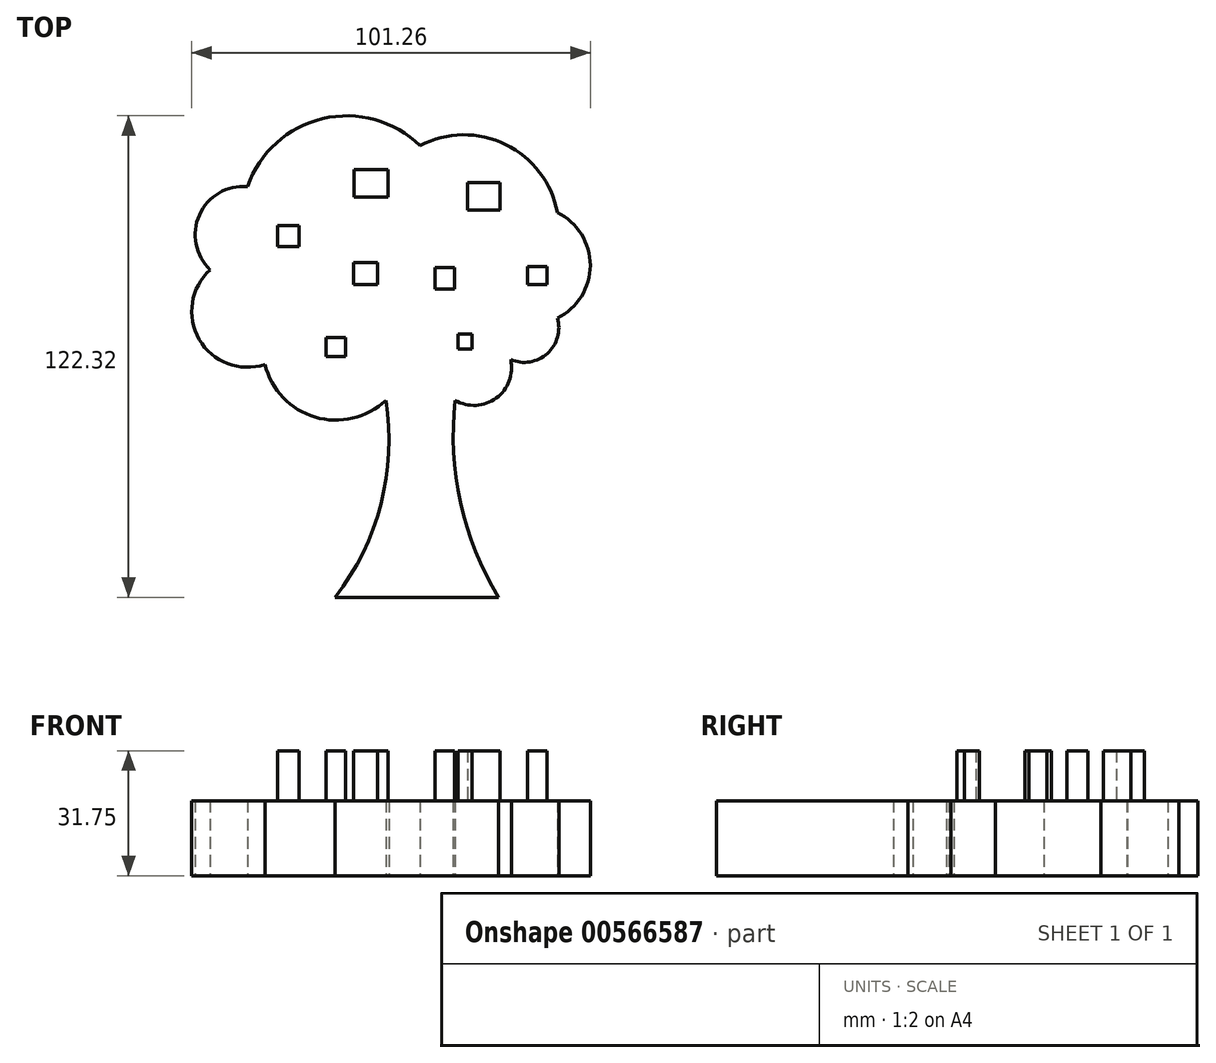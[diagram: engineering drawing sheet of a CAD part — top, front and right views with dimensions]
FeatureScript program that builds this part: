
annotation { "Feature Type Name" : "Feature", "Feature Type Description" : "" }
export const myFeature = defineFeature(function(context is Context, id is Id, definition is map)
    precondition{}
    {
        {
            var Q0;
            Q0=qCreatedBy(makeId("Top.planeOp"),FACE);
            var sketch = newSketch(context, id + "F0", { "sketchPlane" : qUnion([Q0])});
            skArc(sketch, "E0", {"start": v(-21.58, -70.95) * mm, "mid": v(-9.97, -47.28) * mm, "end": v(-8.71, -20.95) * mm});
            skArc(sketch, "E1", {"start": v(8.92, -20.95) * mm, "mid": v(10.25, -46.87) * mm, "end": v(19.92, -70.95) * mm});
            skLineSegment(sketch, "E2", {"start": v(-21.58, -70.95) * mm, "end": v(19.92, -70.95) * mm});
            skArc(sketch, "E3", {"start": v(-39.42, -11.83) * mm, "mid": v(-26.68, -25.19) * mm, "end": v(-8.71, -20.95) * mm});
            skArc(sketch, "E4", {"start": v(-53.32, 12.24) * mm, "mid": v(-56.13, -5.43) * mm, "end": v(-39.42, -11.83) * mm});
            skArc(sketch, "E5", {"start": v(-43.83, 33.4) * mm, "mid": v(-56.09, 26.19) * mm, "end": v(-53.32, 12.24) * mm});
            skArc(sketch, "E6", {"start": v(0, 43.77) * mm, "mid": v(-24.77, 50.66) * mm, "end": v(-43.83, 33.4) * mm});
            skArc(sketch, "E7", {"start": v(34.85, 26.76) * mm, "mid": v(21.74, 44.1) * mm, "end": v(0, 43.77) * mm});
            skArc(sketch, "E8", {"start": v(34.85, 0) * mm, "mid": v(43.23, 13.38) * mm, "end": v(34.85, 26.76) * mm});
            skArc(sketch, "E9", {"start": v(23.03, -10.58) * mm, "mid": v(32.3, -9.04) * mm, "end": v(34.85, 0) * mm});
            skArc(sketch, "E10", {"start": v(8.92, -20.95) * mm, "mid": v(19.33, -20.33) * mm, "end": v(23.03, -10.58) * mm});
            skSolve(sketch);
        }
        {
            var Q0;
            Q0 = qSketchRegion(id + "F0", true);
            extrude(context, id + "F1", {"entities" : qUnion([Q0]), "depth" : 19.05 * mm, "offsetDistance" : 25.4 * mm});
        }
        {
            var Q0;
            Q0=makeQuery(id+"F1.opExtrude","CAP_FACE",FACE,{"disambiguationData":[OSD([sQuery(id+"F0.wireOp",EDGE,"E0"),sQuery(id+"F0.wireOp",EDGE,"E1"),sQuery(id+"F0.wireOp",EDGE,"E2"),sQuery(id+"F0.wireOp",EDGE,"E3"),sQuery(id+"F0.wireOp",EDGE,"E4"),sQuery(id+"F0.wireOp",EDGE,"E5"),sQuery(id+"F0.wireOp",EDGE,"E6"),sQuery(id+"F0.wireOp",EDGE,"E7"),sQuery(id+"F0.wireOp",EDGE,"E8"),sQuery(id+"F0.wireOp",EDGE,"E9"),sQuery(id+"F0.wireOp",EDGE,"E10")])],"isStart":false});
            var sketch = newSketch(context, id + "F2", { "sketchPlane" : qUnion([Q0])});
            skLineSegment(sketch, "E11.bottom", {"start": v(-30.77, 18.09) * mm, "end": v(-36.17, 18.09) * mm});
            skLineSegment(sketch, "E11.top", {"start": v(-30.77, 23.48) * mm, "end": v(-36.17, 23.48) * mm});
            skLineSegment(sketch, "E11.left", {"start": v(-30.77, 18.09) * mm, "end": v(-30.77, 23.48) * mm});
            skLineSegment(sketch, "E11.right", {"start": v(-36.17, 18.09) * mm, "end": v(-36.17, 23.48) * mm});
            skPoint(sketch, "E11.middle", {"position": v(-33.47, 20.78) * mm});
            skLineSegment(sketch, "E12.bottom", {"start": v(8.73, 12.81) * mm, "end": v(3.82, 12.81) * mm});
            skLineSegment(sketch, "E12.top", {"start": v(8.73, 7.41) * mm, "end": v(3.82, 7.41) * mm});
            skLineSegment(sketch, "E12.left", {"start": v(8.73, 12.81) * mm, "end": v(8.73, 7.41) * mm});
            skLineSegment(sketch, "E12.right", {"start": v(3.82, 12.81) * mm, "end": v(3.82, 7.41) * mm});
            skPoint(sketch, "E12.middle", {"position": v(6.28, 10.11) * mm});
            skLineSegment(sketch, "E13.bottom", {"start": v(20.33, 27.38) * mm, "end": v(12.03, 27.38) * mm});
            skLineSegment(sketch, "E13.top", {"start": v(20.33, 34.44) * mm, "end": v(12.03, 34.44) * mm});
            skLineSegment(sketch, "E13.left", {"start": v(20.33, 27.38) * mm, "end": v(20.33, 34.44) * mm});
            skLineSegment(sketch, "E13.right", {"start": v(12.03, 27.38) * mm, "end": v(12.03, 34.44) * mm});
            skPoint(sketch, "E13.middle", {"position": v(16.18, 30.91) * mm});
            skLineSegment(sketch, "E14.bottom", {"start": v(-8.1, 37.76) * mm, "end": v(-16.8, 37.76) * mm});
            skLineSegment(sketch, "E14.top", {"start": v(-8.1, 30.7) * mm, "end": v(-16.8, 30.7) * mm});
            skLineSegment(sketch, "E14.left", {"start": v(-8.1, 37.76) * mm, "end": v(-8.1, 30.7) * mm});
            skLineSegment(sketch, "E14.right", {"start": v(-16.8, 37.76) * mm, "end": v(-16.8, 30.7) * mm});
            skPoint(sketch, "E14.middle", {"position": v(-12.45, 34.23) * mm});
            skLineSegment(sketch, "E15.bottom", {"start": v(-18.91, -9.8) * mm, "end": v(-23.87, -9.8) * mm});
            skLineSegment(sketch, "E15.top", {"start": v(-18.91, -4.98) * mm, "end": v(-23.87, -4.98) * mm});
            skLineSegment(sketch, "E15.left", {"start": v(-18.91, -9.8) * mm, "end": v(-18.91, -4.98) * mm});
            skLineSegment(sketch, "E15.right", {"start": v(-23.87, -9.8) * mm, "end": v(-23.87, -4.98) * mm});
            skPoint(sketch, "E15.middle", {"position": v(-21.4, -7.4) * mm});
            skLineSegment(sketch, "E16.bottom", {"start": v(-10.85, 8.54) * mm, "end": v(-16.9, 8.54) * mm});
            skLineSegment(sketch, "E16.top", {"start": v(-10.85, 14.14) * mm, "end": v(-16.9, 14.14) * mm});
            skLineSegment(sketch, "E16.left", {"start": v(-10.85, 8.54) * mm, "end": v(-10.85, 14.14) * mm});
            skLineSegment(sketch, "E16.right", {"start": v(-16.9, 8.54) * mm, "end": v(-16.9, 14.14) * mm});
            skPoint(sketch, "E16.middle", {"position": v(-13.88, 11.34) * mm});
            skLineSegment(sketch, "E17.bottom", {"start": v(13.16, -4.03) * mm, "end": v(9.66, -4.03) * mm});
            skLineSegment(sketch, "E17.top", {"start": v(13.16, -7.89) * mm, "end": v(9.66, -7.89) * mm});
            skLineSegment(sketch, "E17.left", {"start": v(13.16, -4.03) * mm, "end": v(13.16, -7.89) * mm});
            skLineSegment(sketch, "E17.right", {"start": v(9.66, -4.03) * mm, "end": v(9.66, -7.89) * mm});
            skPoint(sketch, "E17.middle", {"position": v(11.4, -5.96) * mm});
            skLineSegment(sketch, "E18.bottom", {"start": v(32.27, 8.5) * mm, "end": v(27.26, 8.5) * mm});
            skLineSegment(sketch, "E18.top", {"start": v(32.27, 13.05) * mm, "end": v(27.26, 13.05) * mm});
            skLineSegment(sketch, "E18.left", {"start": v(32.27, 8.5) * mm, "end": v(32.27, 13.05) * mm});
            skLineSegment(sketch, "E18.right", {"start": v(27.26, 8.5) * mm, "end": v(27.26, 13.05) * mm});
            skPoint(sketch, "E18.middle", {"position": v(29.77, 10.77) * mm});
            skSolve(sketch);
        }
        {
            var Q0;
            Q0=makeQuery(id+"F2.imprint","IMPRINT",FACE,{"disambiguationData":[TD([[makeQuery(id+"F2.imprint","IMPRINT",EDGE,{"derivedFrom":sQuery(id+"F2.wireOp",EDGE,"E15.bottom")}),-1.0]])]});
            var Q1;
            Q1=makeQuery(id+"F2.imprint","IMPRINT",FACE,{"disambiguationData":[TD([[makeQuery(id+"F2.imprint","IMPRINT",EDGE,{"derivedFrom":sQuery(id+"F2.wireOp",EDGE,"E16.bottom")}),-1.0]])]});
            var Q2;
            Q2=makeQuery(id+"F2.imprint","IMPRINT",FACE,{"disambiguationData":[TD([[makeQuery(id+"F2.imprint","IMPRINT",EDGE,{"derivedFrom":sQuery(id+"F2.wireOp",EDGE,"E12.bottom")}),1.0]])]});
            var Q3;
            Q3=makeQuery(id+"F2.imprint","IMPRINT",FACE,{"disambiguationData":[TD([[makeQuery(id+"F2.imprint","IMPRINT",EDGE,{"derivedFrom":sQuery(id+"F2.wireOp",EDGE,"E13.bottom")}),-1.0]])]});
            var Q4;
            Q4=makeQuery(id+"F2.imprint","IMPRINT",FACE,{"disambiguationData":[TD([[makeQuery(id+"F2.imprint","IMPRINT",EDGE,{"derivedFrom":sQuery(id+"F2.wireOp",EDGE,"E14.bottom")}),1.0]])]});
            var Q5;
            Q5=makeQuery(id+"F2.imprint","IMPRINT",FACE,{"disambiguationData":[TD([[makeQuery(id+"F2.imprint","IMPRINT",EDGE,{"derivedFrom":sQuery(id+"F2.wireOp",EDGE,"E11.bottom")}),-1.0]])]});
            var Q6;
            Q6=makeQuery(id+"F2.imprint","IMPRINT",FACE,{"disambiguationData":[TD([[makeQuery(id+"F2.imprint","IMPRINT",EDGE,{"derivedFrom":sQuery(id+"F2.wireOp",EDGE,"E17.bottom")}),1.0]])]});
            var Q7;
            Q7=makeQuery(id+"F2.imprint","IMPRINT",FACE,{"disambiguationData":[TD([[makeQuery(id+"F2.imprint","IMPRINT",EDGE,{"derivedFrom":sQuery(id+"F2.wireOp",EDGE,"E18.bottom")}),-1.0]])]});
            extrude(context, id + "F3", {"entities" : qUnion([Q0, Q1, Q2, Q3, Q4, Q5, Q6, Q7]), "operationType" : NewBodyOperationType.ADD, "depth" : 12.7 * mm, "offsetDistance" : 25.4 * mm});
        }
    });
